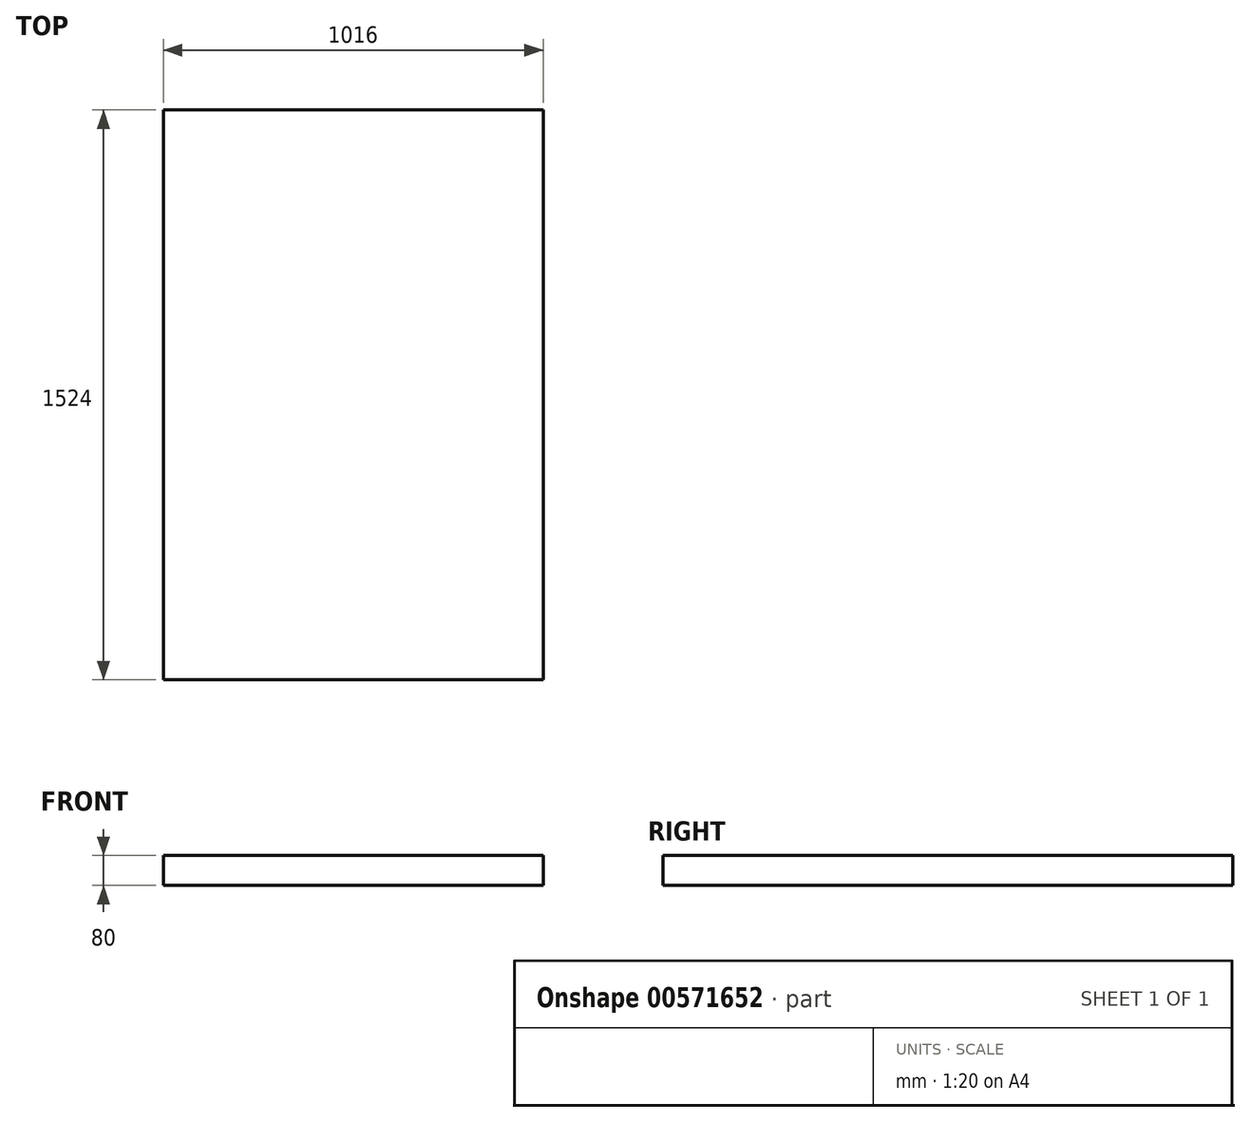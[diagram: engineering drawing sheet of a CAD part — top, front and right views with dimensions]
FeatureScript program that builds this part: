
annotation { "Feature Type Name" : "Feature", "Feature Type Description" : "" }
export const myFeature = defineFeature(function(context is Context, id is Id, definition is map)
    precondition{}
    {
        {
            var Q0;
            Q0=qCreatedBy(makeId("Top.planeOp"),FACE);
            var sketch = newSketch(context, id + "F0", { "sketchPlane" : qUnion([Q0])});
            skLineSegment(sketch, "E0.bottom", {"start": v(0, 0) * mm, "end": v(1016, 0) * mm});
            skLineSegment(sketch, "E0.top", {"start": v(0, -1524) * mm, "end": v(1016, -1524) * mm});
            skLineSegment(sketch, "E0.left", {"start": v(0, 0) * mm, "end": v(0, -1524) * mm});
            skLineSegment(sketch, "E0.right", {"start": v(1016, 0) * mm, "end": v(1016, -1524) * mm});
            skSolve(sketch);
        }
        {
            var Q0;
            Q0=makeQuery(id+"F0.imprint","IMPRINT",FACE,{"disambiguationData":[TD([[makeQuery(id+"F0.imprint","IMPRINT",EDGE,{"derivedFrom":sQuery(id+"F0.wireOp",EDGE,"E0.bottom")}),-1.0]])]});
            extrude(context, id + "F1", {"entities" : qUnion([Q0]), "depth" : 80 * mm, "offsetDistance" : 25.4 * mm});
        }
    });
